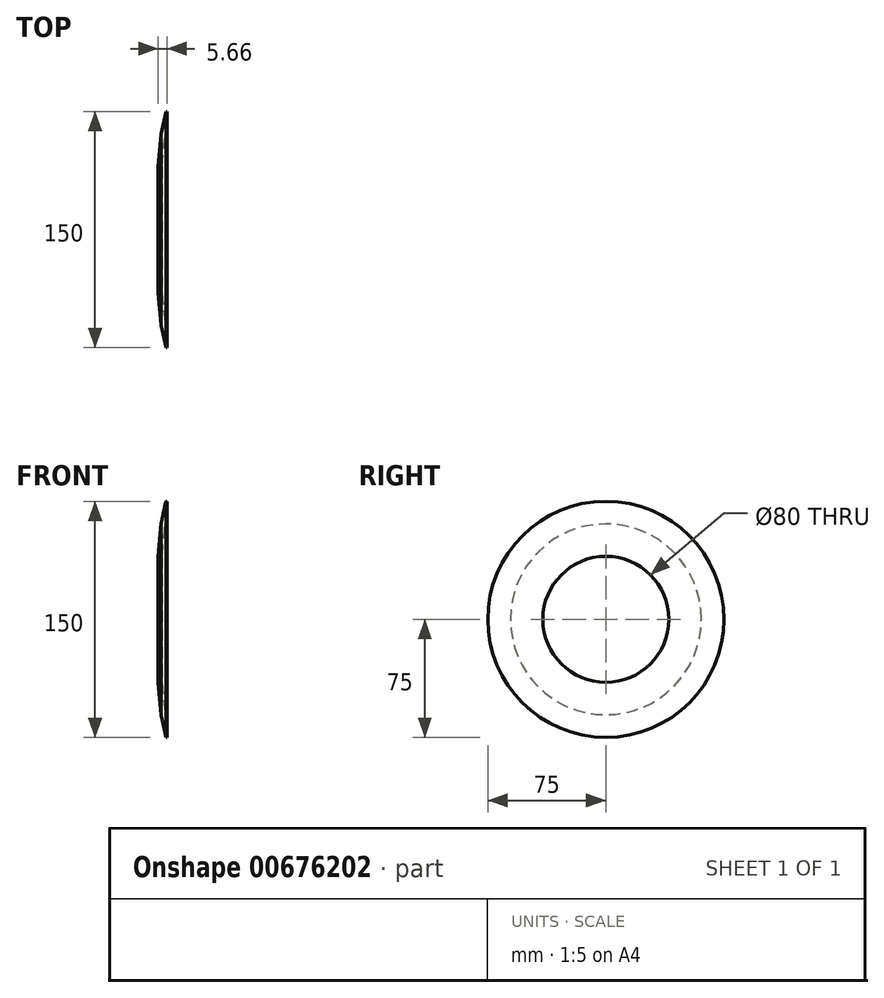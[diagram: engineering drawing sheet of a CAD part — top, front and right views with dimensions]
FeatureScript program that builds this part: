
annotation { "Feature Type Name" : "Feature", "Feature Type Description" : "" }
export const myFeature = defineFeature(function(context is Context, id is Id, definition is map)
    precondition{}
    {
        {
            var Q0;
            Q0=qCreatedBy(makeId("Front.planeOp"),FACE);
            var sketch = newSketch(context, id + "F0", { "sketchPlane" : qUnion([Q0])});
            skLineSegment(sketch, "E0", {"start": v(0, 40) * mm, "end": v(1.8, 60.6) * mm});
            skLineSegment(sketch, "E1", {"start": v(1.8, 60.6) * mm, "end": v(4.86, 75) * mm});
            skLineSegment(sketch, "E2", {"start": v(4.86, 75) * mm, "end": v(5.66, 75) * mm});
            skLineSegment(sketch, "E3", {"start": v(5.66, 75) * mm, "end": v(2.6, 40) * mm});
            skLineSegment(sketch, "E4", {"start": v(2.6, 40) * mm, "end": v(0, 40) * mm});
            skLineSegment(sketch, "E5", {"start": v(0, 0) * mm, "end": v(19.64, 0) * mm, "construction": true});
            skSolve(sketch);
        }
        {
            var Q0;
            Q0=makeQuery(id+"F0.imprint","IMPRINT",FACE,{"disambiguationData":[TD([[makeQuery(id+"F0.imprint","IMPRINT",EDGE,{"derivedFrom":sQuery(id+"F0.wireOp",EDGE,"E0")}),-1.0]])]});
            var Q1;
            Q1=sQuery(id+"F0.wireOp",EDGE,"E5");
            revolve(context, id + "F1", {"entities" : qUnion([Q0]), "axis" : qUnion([Q1]), "revolveType" : RevolveType.FULL});
        }
    });
